# Revit family: 44190300(2023)
name_source: partatom
category: Plumbing Fixtures
units: mm (PartAtom-declared; Revit-internal decimal feet)

## family parameters
Always vertical = Yes
Cut with Voids When Loaded = No
OmniClass Number = 23.45.55.00
OmniClass Title = Sanitary Faucets, Wastes
Part Type = Normal
Room Calculation Point = No
Round Connector Dimension = Use Diameter
Shared = No
Work Plane-Based = No

## types (1)
- 44190300 Overhead shower set
    2D/3D/BIM Files URL = http://static.hansa.com
    3D View = https://static.hansa.com
    Advanced Features = Flexible length / can be shortened;Hose guide, revolving
    AssetType = Fixed
    BIMObjectName = 44190300(2023)
    Backflow Prevention EN1717 = EB
    BodyMaterial = Brass
    Brand = HANSA
    Catalog Drawing URL = http://static.hansa.com
    CloseOffRating = 0
    Color = Chrome
    Connection = Straight coupling(s);Direct connection;External thread
    Connection Size = G1/2
    Default Elevation = 0 mm  [stored 0 ft]
    Dimension Drawing URL = http://static.hansa.com
    Diverter = Turn operated diverter
    DurationUnit = Year
    EAN Number = 4057304018015
    EN Standard = EN1112
    ETIM Class Number = EC010109 Sliding rod combination
    FDV Document URL = http://www.hansa.com
    FaucetMainMaterial = Brass
    Finish = Polished
    Flow Drawing URL = http://static.hansa.com
    Flow Rate At 300kPa With Flow Controller = 0.3 L/s
    FlowCoefficient = 0
    Group = Shower set
    Hand Shower Size = Ø110
    IfcExportAs = IfcValveType
    IfcExportType = FAUCET
    Installation Type = Wall mounted
    Installation and Maintenance Guide URL = http://static.hansa.com
    Interactive AR View URL = https://static.hansa.com
    Manufacturer = HANSA
    ManufacturerName = HANSA
    ManufacturerURL = http://www.hansa.com
    Market = Austria;Belgium;Czech Republic;Germany;Spain;France;International;Italy;Netherlands;Slovakia
    Material = Brass/Plastic
    Max. Hot Water Supply = 65 °C
    Mechanical Parts = Non-return valve(s)
    Mobile Product Information URL = http://mpi.hansa.com
    Model = 44190300 Overhead shower set
    ModelReference = 44190300
    NBSDescription = Shower mixers
    NBSReference = 45-35-70/335
    Name = 44190300 Overhead shower set
    Name_en = 44190300 Overhead shower set
    Noise Class = II (ISO 3822)
    NominalDepth = 581 mm
    NominalHeight = 1223 mm
    NominalWidth = 250 mm
    Over Head Shower Size = Ø250
    Pressure Loss With Flow 02ls = 250000.0 Pa
    Product Code = 44190300
    Product Family = HANSAVIVA
    Product Image URL = http://static.hansa.com
    Product URL = http://static.hansa.com
    Sales Package dimensions (LxWxH) = 1120 x 264 x 74
    Shape = Sculptured
    Shower Parts = Rotatable ball joint connection;Hand shower;;Adjustable shower rail bracket;;Shower hose (1750 mm);Shower rail;Anti limescale technology (easy to clean);Twist guard for shower hose;Variable fixing points
    Shower Spray = Normal;Massage;Rain
    Shower Spray Number = 3 shower sprays
    Size = 95 x 60 x 245 mm
    Surface treatment = Chrome
    Technical DataSheet URL = http://www.hansa.com
    UNSPSC Class Number = 30181503 Showers
    URL Declaration Of Performance (DOP) = http://static.hansa.com
    URL Declaration of Asbestos = http://static.hansa.com
    URL Declaration of Conformity = http://static.hansa.com
    URL Declaration of SCIP = http://static.hansa.com
    URL EU Packaging Declaration = http://static.hansa.com
    URL EcoLabel Declaration = http://static.hansa.com
    URL REACH = http://static.hansa.com
    Uniclass2 = Pr_40_30_96_81
    Uniclass2015Description = Shower thermostatic water supply sets
    Uniclass2015Reference = Pr_40_20_87_81
    Version = 1
    VersionDate = 01/06/2023
    Warranty Information URL = http://warranty.hansa.com
    WarrantyDescription = http://warranty.hansa.com
    WarrantyDurationUnit = Year
    Working Pressure = 50 - 500 kPa

note: [stored X ft] marks values corroborated as IEEE doubles in the binary element streams (Revit-internal decimal feet)

## geometry (parser evidence)
native form markers: Sweep x6
no freeform markers — native parametric forms only
